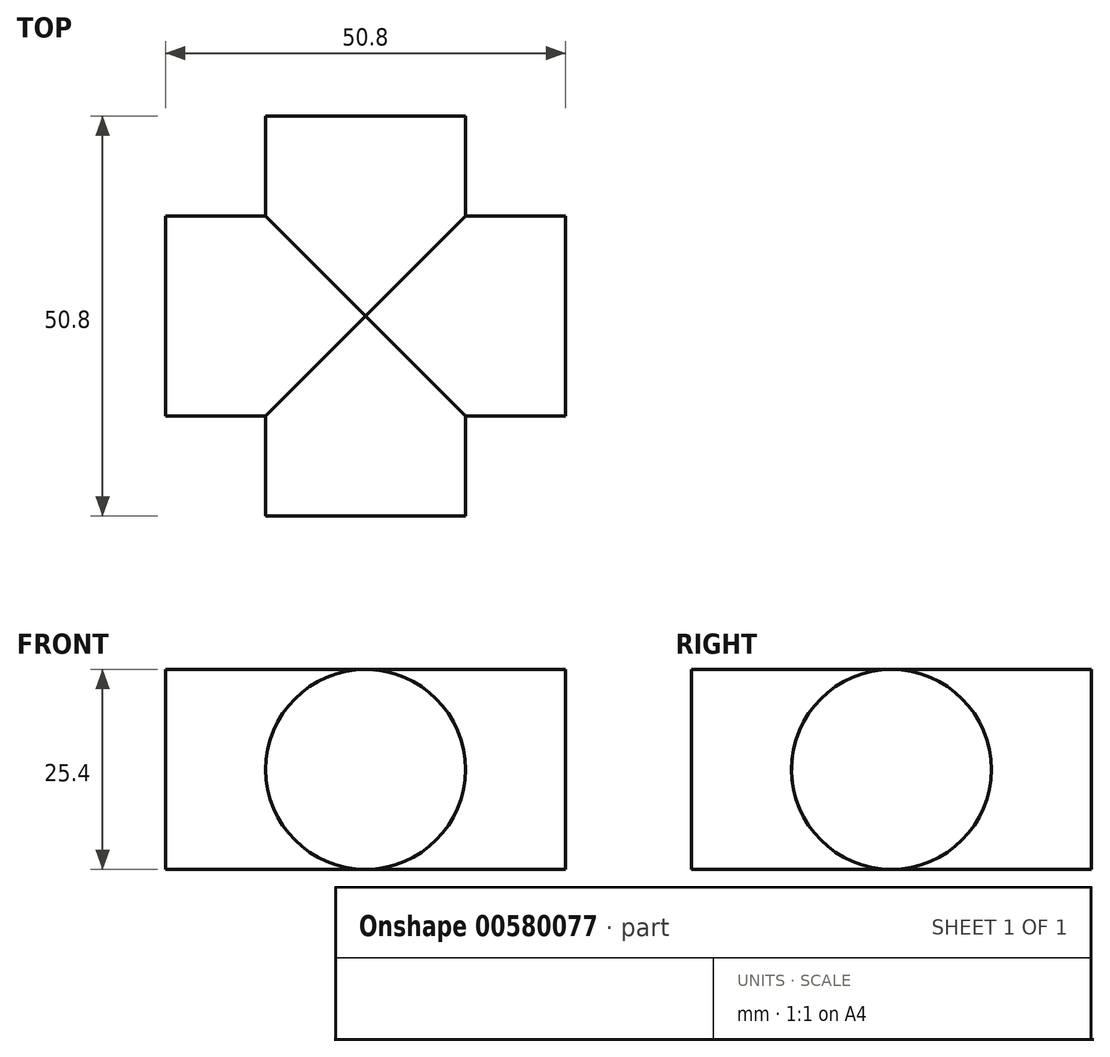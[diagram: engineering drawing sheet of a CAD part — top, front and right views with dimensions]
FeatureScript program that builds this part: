
annotation { "Feature Type Name" : "Feature", "Feature Type Description" : "" }
export const myFeature = defineFeature(function(context is Context, id is Id, definition is map)
    precondition{}
    {
        {
            var Q0;
            Q0=qCreatedBy(makeId("Front.planeOp"),FACE);
            var sketch = newSketch(context, id + "F0", { "sketchPlane" : qUnion([Q0])});
            skCircle(sketch, "E0", {"center": v(0, 0) * mm, "radius": 12.7 * mm});
            skSolve(sketch);
        }
        {
            var Q0;
            Q0=makeQuery(id+"F0.imprint","IMPRINT",FACE,{"disambiguationData":[TD([[makeQuery(id+"F0.imprint","IMPRINT",EDGE,{"derivedFrom":sQuery(id+"F0.wireOp",EDGE,"E0")}),1.0]])]});
            extrude(context, id + "F1", {"entities" : qUnion([Q0]), "endBound" : BoundingType.SYMMETRIC, "depth" : 50.8 * mm, "offsetDistance" : 25.4 * mm});
        }
        {
            var Q0;
            Q0=qCreatedBy(makeId("Right.planeOp"),FACE);
            var sketch = newSketch(context, id + "F2", { "sketchPlane" : qUnion([Q0])});
            skCircle(sketch, "E1", {"center": v(0, 0) * mm, "radius": 12.7 * mm});
            skSolve(sketch);
        }
        {
            var Q0;
            Q0 = qSketchRegion(id + "F2", true);
            extrude(context, id + "F3", {"entities" : qUnion([Q0]), "operationType" : NewBodyOperationType.ADD, "endBound" : BoundingType.SYMMETRIC, "depth" : 50.8 * mm, "offsetDistance" : 25.4 * mm});
        }
    });
